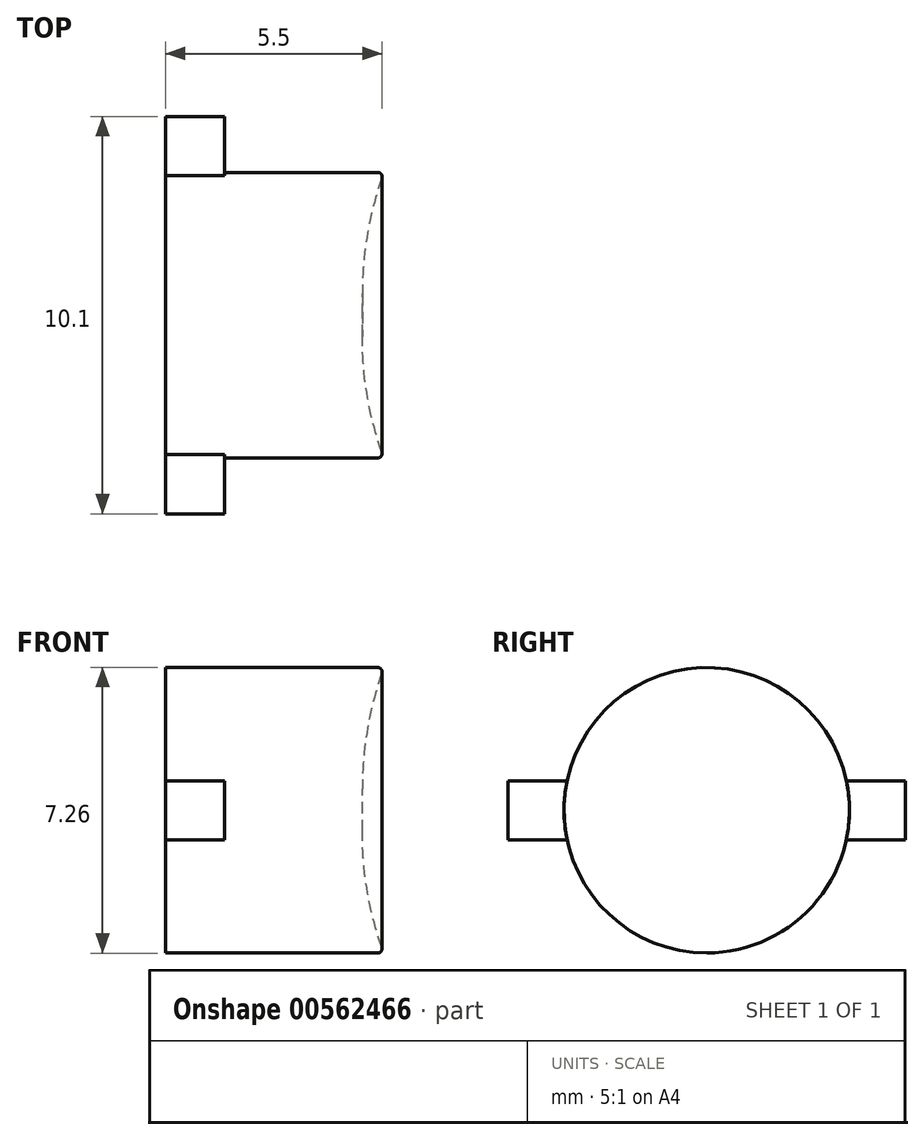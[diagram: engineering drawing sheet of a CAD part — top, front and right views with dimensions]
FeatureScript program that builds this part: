
annotation { "Feature Type Name" : "Feature", "Feature Type Description" : "" }
export const myFeature = defineFeature(function(context is Context, id is Id, definition is map)
    precondition{}
    {
        {
            var Q0;
            Q0=qCreatedBy(makeId("Right.planeOp"),FACE);
            var sketch = newSketch(context, id + "F0", { "sketchPlane" : qUnion([Q0])});
            skCircle(sketch, "E0", {"center": v(0, 0) * mm, "radius": 3.62 * mm});
            skSolve(sketch);
        }
        {
            var Q0;
            Q0=makeQuery(id+"F0.imprint","IMPRINT",FACE,{"disambiguationData":[TD([[makeQuery(id+"F0.imprint","IMPRINT",EDGE,{"derivedFrom":sQuery(id+"F0.wireOp",EDGE,"E0")}),1.0]])]});
            extrude(context, id + "F1", {"entities" : qUnion([Q0]), "depth" : 5.5 * mm, "offsetDistance" : 25 * mm, "symmetric" : true});
        }
        {
            var Q0;
            Q0=makeQuery(id+"F1.opExtrude","CAP_FACE",FACE,{"disambiguationData":[OSD([sQuery(id+"F0.wireOp",EDGE,"E0")])],"isStart":true});
            var sketch = newSketch(context, id + "F2", { "sketchPlane" : qUnion([Q0])});
            skLineSegment(sketch, "E1.left", {"start": v(5.05, -0.75) * mm, "end": v(5.05, 0.75) * mm});
            skLineSegment(sketch, "E2.left", {"start": v(-5.05, 0.75) * mm, "end": v(-5.05, -0.75) * mm});
            skLineSegment(sketch, "E3", {"start": v(5.05, 0.75) * mm, "end": v(3.55, 0.75) * mm});
            skLineSegment(sketch, "E4", {"start": v(5.05, -0.75) * mm, "end": v(3.55, -0.75) * mm});
            skArc(sketch, "E5", {"start": v(-3.55, 0.75) * mm, "mid": v(-3.63, 0) * mm, "end": v(-3.55, -0.75) * mm});
            skLineSegment(sketch, "E6", {"start": v(-5.05, 0.75) * mm, "end": v(-3.55, 0.75) * mm});
            skLineSegment(sketch, "E7", {"start": v(-5.05, -0.75) * mm, "end": v(-3.55, -0.75) * mm});
            skArc(sketch, "E8.trimOffspring", {"start": v(3.55, -0.75) * mm, "mid": v(3.63, 0) * mm, "end": v(3.55, 0.75) * mm});
            skPoint(sketch, "E9", {"position": v(5.05, 0) * mm});
            skPoint(sketch, "E10", {"position": v(-5.05, 0) * mm});
            skSolve(sketch);
        }
        {
            var Q0;
            Q0=qSketchRegion(id+"F2",true);
            extrude(context, id + "F3", {"entities" : qUnion([Q0]), "operationType" : NewBodyOperationType.ADD, "oppositeDirection" : true, "depth" : 1.5 * mm, "offsetDistance" : 25 * mm});
        }
        {
            var Q0;
            Q0=makeQuery(id+"F1.opExtrude","CAP_FACE",FACE,{"disambiguationData":[OSD([sQuery(id+"F0.wireOp",EDGE,"E0")])],"isStart":false});
            var sketch = newSketch(context, id + "F4", { "sketchPlane" : qUnion([Q0])});
            skCircle(sketch, "E11", {"center": v(0, 0) * mm, "radius": 3.5 * mm});
            skSolve(sketch);
        }
        {
            var Q0;
            Q0=qSketchRegion(id+"F4",true);
            extrude(context, id + "F5", {"entities" : qUnion([Q0]), "operationType" : NewBodyOperationType.REMOVE, "oppositeDirection" : true, "depth" : .5 * mm, "offsetDistance" : 25 * mm});
        }
        {
            var Q0;
            Q0=makeQuery(id+"F5.boolean.opBoolean","COPY",FACE,{"derivedFrom":makeQuery(id+"F5.opExtrude","CAP_FACE",FACE,{"disambiguationData":[OSD([sQuery(id+"F4.wireOp",EDGE,"E11")])],"isStart":false})});
            fillet(context, id + "F6", {"entities" : qUnion([Q0]), "radius" : 9 * mm, "tangentPropagation" : true, "allowEdgeOverflow" : false});
        }
        {
            var Q0;
            Q0=makeQuery(id+"F6.opFillet","BLEND_EDGE",EDGE,{"blendedFrom":[makeQuery(id+"F5.boolean.opBoolean","COPY",EDGE,{"derivedFrom":makeQuery(id+"F5.opExtrude","CAP_EDGE",EDGE,{"disambiguationData":[OSD([sQuery(id+"F4.wireOp",EDGE,"E11")])],"isStart":false})}),makeQuery(id+"F1.opExtrude","CAP_FACE",FACE,{"disambiguationData":[OSD([sQuery(id+"F0.wireOp",EDGE,"E0")])],"isStart":false})],"blendedInto":[makeQuery(id+"F1.opExtrude","CAP_FACE",FACE,{"disambiguationData":[OSD([sQuery(id+"F0.wireOp",EDGE,"E0")])],"isStart":false})]});
            var Q1;
            Q1=makeQuery(id+"F1.opExtrude","CAP_EDGE",EDGE,{"disambiguationData":[OSD([sQuery(id+"F0.wireOp",EDGE,"E0")])],"isStart":false});
            fillet(context, id + "F7", {"entities" : qUnion([Q0, Q1]), "radius" : .1 * mm, "tangentPropagation" : true, "allowEdgeOverflow" : false});
        }
    });
